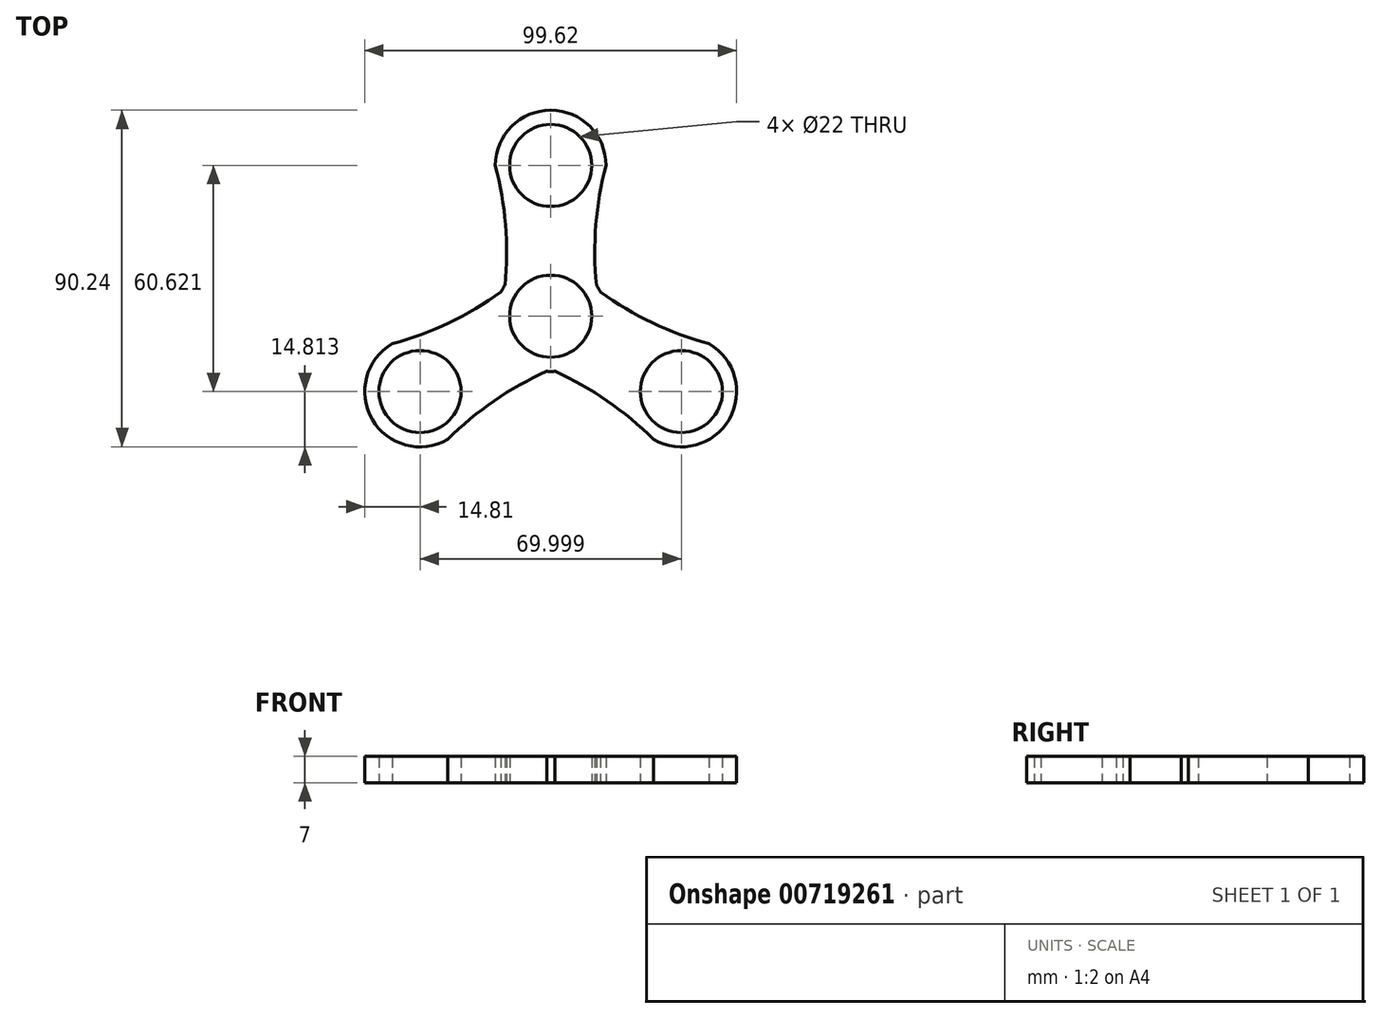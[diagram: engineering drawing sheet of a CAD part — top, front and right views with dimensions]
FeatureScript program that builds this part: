
annotation { "Feature Type Name" : "Feature", "Feature Type Description" : "" }
export const myFeature = defineFeature(function(context is Context, id is Id, definition is map)
    precondition{}
    {
        {
            var Q0;
            Q0=qCreatedBy(makeId("Top.planeOp"),FACE);
            var sketch = newSketch(context, id + "F0", { "sketchPlane" : qUnion([Q0])});
            skCircle(sketch, "E0", {"center": v(0, 0) * mm, "radius": 11 * mm});
            skCircle(sketch, "E1", {"center": v(0, 40.41) * mm, "radius": 11 * mm});
            skArc(sketch, "E2.0", {"start": v(14.8, 40.41) * mm, "mid": v(0, 55.22) * mm, "end": v(-14.8, 40.41) * mm});
            skArc(sketch, "E3.0", {"start": v(-12.25, 8.32) * mm, "mid": v(-12.82, 7.4) * mm, "end": v(-13.33, 6.44) * mm});
            skLineSegment(sketch, "E4.trimOffspring", {"start": v(-11, 40.41) * mm, "end": v(11, 40.41) * mm});
            skArc(sketch, "E5", {"start": v(-12.25, 8.32) * mm, "mid": v(-12.1, 24.48) * mm, "end": v(-14.8, 40.41) * mm});
            skArc(sketch, "E6.MirrorCS", {"start": v(12.25, 8.32) * mm, "mid": v(12.1, 24.48) * mm, "end": v(14.8, 40.41) * mm});
            skArc(sketch, "E7.1.0", {"start": v(-13.33, 6.44) * mm, "mid": v(-27.25, -1.77) * mm, "end": v(-42.4, -7.38) * mm});
            skCircle(sketch, "E7.1.1", {"center": v(-35, -20.2) * mm, "radius": 11 * mm});
            skArc(sketch, "E7.1.2", {"start": v(-1.09, -14.77) * mm, "mid": v(-15.16, -22.72) * mm, "end": v(-27.6, -33.03) * mm});
            skArc(sketch, "E7.1.3", {"start": v(-42.4, -7.38) * mm, "mid": v(-47.82, -27.61) * mm, "end": v(-27.6, -33.03) * mm});
            skArc(sketch, "E7.2.0", {"start": v(1.09, -14.77) * mm, "mid": v(15.16, -22.72) * mm, "end": v(27.6, -33.03) * mm});
            skCircle(sketch, "E7.2.1", {"center": v(35, -20.2) * mm, "radius": 11 * mm});
            skArc(sketch, "E7.2.2", {"start": v(13.33, 6.44) * mm, "mid": v(27.25, -1.77) * mm, "end": v(42.4, -7.38) * mm});
            skArc(sketch, "E7.2.3", {"start": v(27.6, -33.03) * mm, "mid": v(47.82, -27.61) * mm, "end": v(42.4, -7.38) * mm});
            skArc(sketch, "E8.trimOffspring", {"start": v(13.33, 6.44) * mm, "mid": v(12.82, 7.4) * mm, "end": v(12.25, 8.32) * mm});
            skArc(sketch, "E9.trimOffspring", {"start": v(-1.09, -14.77) * mm, "mid": v(0, -14.8) * mm, "end": v(1.09, -14.77) * mm});
            skSolve(sketch);
        }
        {
            var Q0;
            Q0=makeQuery(id+"F0.imprint","IMPRINT",FACE,{"disambiguationData":[TD([[makeQuery(id+"F0.imprint","IMPRINT",EDGE,{"derivedFrom":sQuery(id+"F0.wireOp",EDGE,"E0")}),-1.0]])]});
            extrude(context, id + "F1", {"entities" : qUnion([Q0]), "depth" : 7 * mm, "offsetDistance" : 25.4 * mm});
        }
    });
